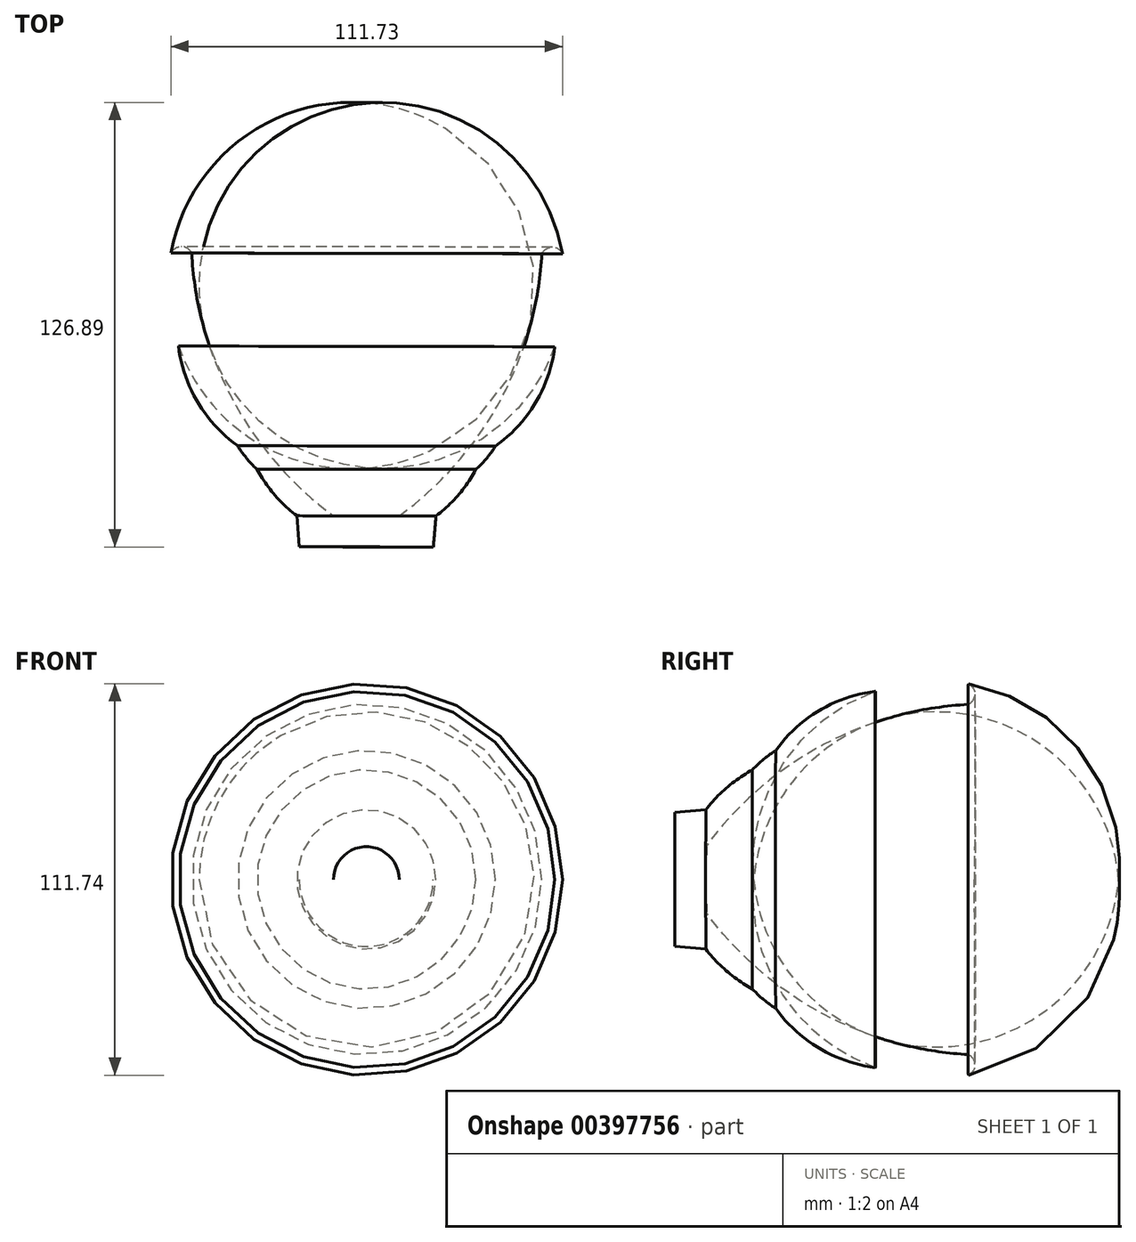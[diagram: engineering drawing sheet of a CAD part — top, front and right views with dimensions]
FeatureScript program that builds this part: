
annotation { "Feature Type Name" : "Feature", "Feature Type Description" : "" }
export const myFeature = defineFeature(function(context is Context, id is Id, definition is map)
    precondition{}
    {
        {
            var Q0;
            Q0=qCreatedBy(makeId("Top.planeOp"),FACE);
            var sketch = newSketch(context, id + "F0", { "sketchPlane" : qUnion([Q0])});
            skLineSegment(sketch, "E0", {"start": v(0, -48.3) * mm, "end": v(10.5, -48.3) * mm});
            skArc(sketch, "E1", {"start": v(10.5, -48.3) * mm, "mid": v(16.92, -42.27) * mm, "end": v(21.94, -35.03) * mm});
            skArc(sketch, "E2", {"start": v(21.94, -35.03) * mm, "mid": v(24.93, -31.9) * mm, "end": v(27.47, -28.4) * mm});
            skArc(sketch, "E3", {"start": v(27.47, -28.4) * mm, "mid": v(38.92, -15.97) * mm, "end": v(44.43, 0) * mm});
            skPoint(sketch, "E4.end.orphan", {"position": v(44.43, 5.9) * mm});
            skArc(sketch, "E5", {"start": v(44.43, 0) * mm, "mid": v(47.26, 13.13) * mm, "end": v(46.64, 26.55) * mm});
            skArc(sketch, "E6", {"start": v(46.64, 26.55) * mm, "mid": v(43.7, 28.41) * mm, "end": v(40.74, 26.55) * mm});
            skArc(sketch, "E7", {"start": v(0, -48.3) * mm, "mid": v(28.8, -15.46) * mm, "end": v(40.74, 26.55) * mm});
            skLineSegment(sketch, "E8", {"start": v(0, -48.3) * mm, "end": v(5.25, -48.3) * mm});
            skLineSegment(sketch, "E9", {"start": v(5.25, -48.3) * mm, "end": v(0, -48.3) * mm});
            skPoint(sketch, "E10.end.orphan", {"position": v(24.52, -48.3) * mm});
            skPoint(sketch, "E11.end.orphan", {"position": v(-9.4, -57.15) * mm});
            skPoint(sketch, "E12.orphan", {"position": v(-9.4, -48.3) * mm});
            skArc(sketch, "E13", {"start": v(0, -48.3) * mm, "mid": v(-6.46, -50.86) * mm, "end": v(-9.4, -57.15) * mm});
            skLineSegment(sketch, "E14", {"start": v(-9.4, -48.3) * mm, "end": v(0, -48.3) * mm});
            skLineSegment(sketch, "E15", {"start": v(-9.4, -48.3) * mm, "end": v(-9.4, -57.15) * mm});
            skLineSegment(sketch, "E16", {"start": v(9.77, -57.15) * mm, "end": v(10.5, -48.3) * mm});
            skLineSegment(sketch, "E17", {"start": v(-9.4, -57.15) * mm, "end": v(9.77, -57.15) * mm});
            skLineSegment(sketch, "E18", {"start": v(-9.4, 11.43) * mm, "end": v(-9.25, 8.5) * mm});
            skLineSegment(sketch, "E19", {"start": v(-9.4, -78.9) * mm, "end": v(-9.25, 8.5) * mm});
            skPoint(sketch, "E20.end.orphan", {"position": v(-15.3, -57.15) * mm});
            skPoint(sketch, "E21.start.orphan", {"position": v(-4.81, -79.27) * mm});
            skSolve(sketch);
        }
        {
            var Q0;
            Q0=makeQuery(id+"F0.imprint","IMPRINT",FACE,{"disambiguationData":[TD([[makeQuery(id+"F0.imprint","IMPRINT",EDGE,{"derivedFrom":sQuery(id+"F0.wireOp",EDGE,"E0")}),1.0]])]});
            var Q1;
            Q1=makeQuery(id+"F0.imprint","IMPRINT",FACE,{"disambiguationData":[TD([[makeQuery(id+"F0.imprint","IMPRINT",EDGE,{"derivedFrom":sQuery(id+"F0.wireOp",EDGE,"E0")}),-1.0]])]});
            var Q2;
            {var subQ0=sQuery(id+"F0.wireOp",EDGE,"E14");var subQ3=sQuery(id+"F0.wireOp",EDGE,"E19");var subQ5=makeQuery(id+"F0.imprint","INTERSECT",VERTEX,{"derivedFrom":[subQ0,subQ3]});Q2=makeQuery(id+"F0.imprint","IMPRINT",FACE,{"disambiguationData":[TD([[makeQuery(id+"F0.imprint","IMPRINT",EDGE,{"disambiguationData":[TD([[subQ5,1.0]])],"derivedFrom":subQ3}),-1.0]])]});}
            var Q3;
            Q3=sQuery(id+"F0.wireOp",EDGE,"E19");
            revolve(context, id + "F1", {"entities" : qUnion([Q0, Q1, Q2]), "axis" : qUnion([Q3]), "revolveType" : RevolveType.FULL});
        }
    });
